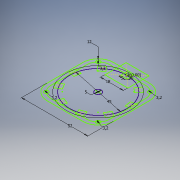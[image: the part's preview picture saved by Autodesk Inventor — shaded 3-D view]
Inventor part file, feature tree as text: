
AUTODESK INVENTOR PART (.ipt)
format: ipt  version: 2018 (Build 220112000, 112)  size: 123,392 bytes
history: native  units: mm
features: sketch x1
ambient origin geometry x8: Origin, YZ Plane, XZ Plane, XY Plane, X Axis, Y Axis, Z Axis, Center Point
feature tree (1):
  sketch  "Skizze1"  dims[d2=12.0mm d3=45.0mm d7=18.0mm d12=5.0mm d13=3.0mm d14=3.2mm d15=3.2mm d16=3.2mm d17=3.2mm d18=52.0mm d19=5.0mm d20=5.0mm d21=90.0mm d23=360.0deg]
